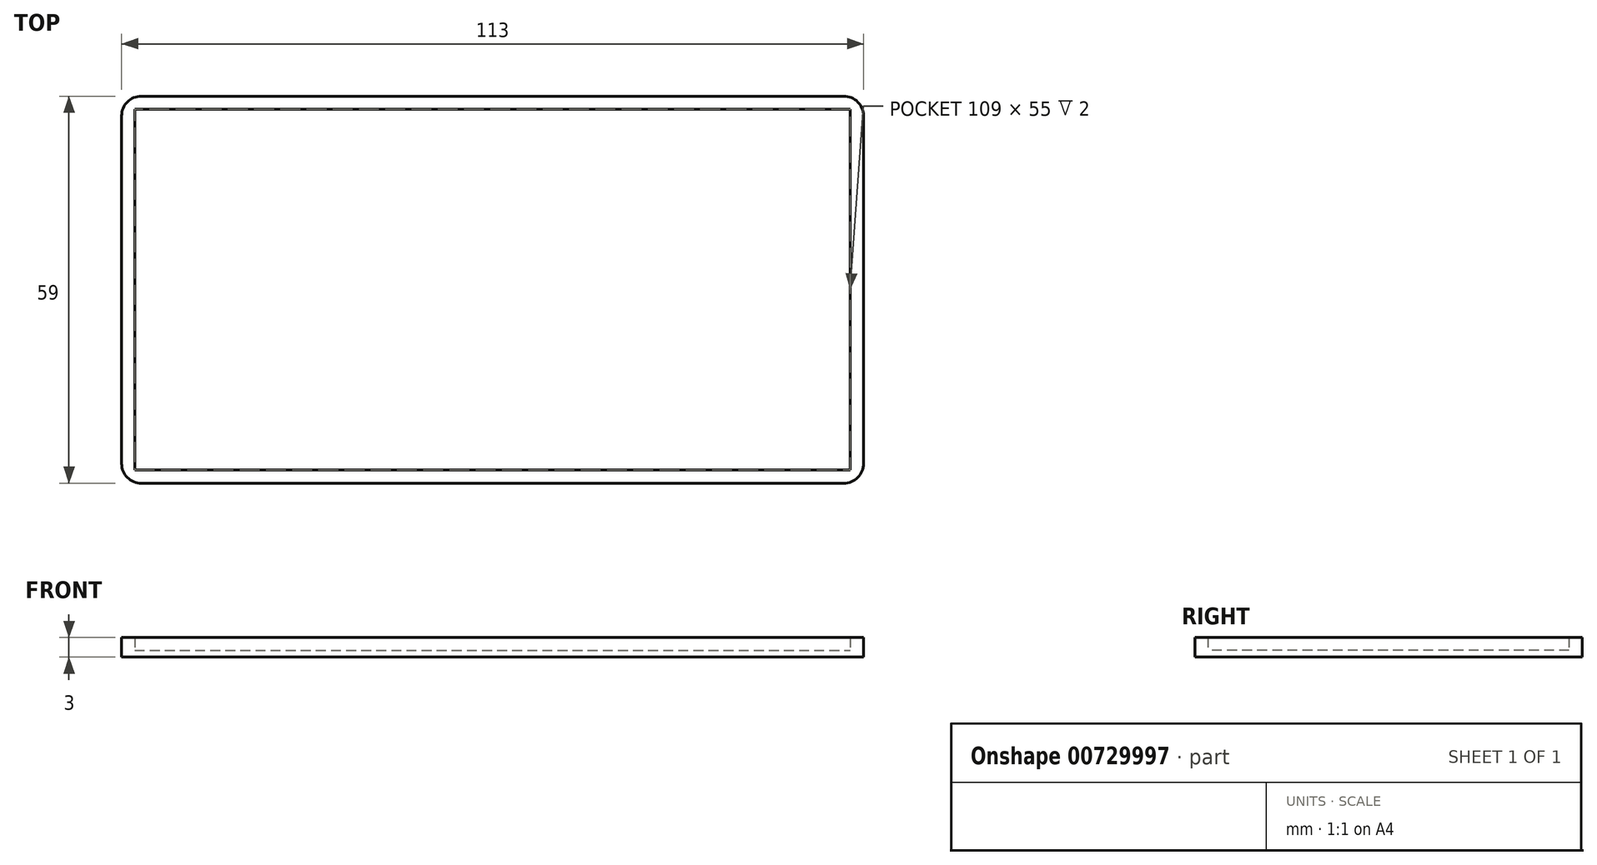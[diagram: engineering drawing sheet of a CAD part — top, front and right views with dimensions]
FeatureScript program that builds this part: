
annotation { "Feature Type Name" : "Feature", "Feature Type Description" : "" }
export const myFeature = defineFeature(function(context is Context, id is Id, definition is map)
    precondition{}
    {
        {
            var Q0;
            Q0=qCreatedBy(makeId("Top.planeOp"),FACE);
            var sketch = newSketch(context, id + "F0", { "sketchPlane" : qUnion([Q0])});
            skLineSegment(sketch, "E0.bottom", {"start": v(-54.5, 23.85) * mm, "end": v(54.5, 23.85) * mm});
            skLineSegment(sketch, "E0.top", {"start": v(-54.5, -31.15) * mm, "end": v(54.5, -31.15) * mm});
            skLineSegment(sketch, "E0.left", {"start": v(-54.5, 23.85) * mm, "end": v(-54.5, -31.15) * mm});
            skLineSegment(sketch, "E0.right", {"start": v(54.5, 23.85) * mm, "end": v(54.5, -31.15) * mm});
            skLineSegment(sketch, "E1.bottom", {"start": v(-56.5, 25.85) * mm, "end": v(56.5, 25.85) * mm});
            skLineSegment(sketch, "E1.top", {"start": v(-56.5, -33.15) * mm, "end": v(56.5, -33.15) * mm});
            skLineSegment(sketch, "E1.left", {"start": v(-56.5, 25.85) * mm, "end": v(-56.5, -33.15) * mm});
            skLineSegment(sketch, "E1.right", {"start": v(56.5, 25.85) * mm, "end": v(56.5, -33.15) * mm});
            skArc(sketch, "E2", {"start": v(-10, -33.15) * mm, "mid": v(0, -43.15) * mm, "end": v(10, -33.15) * mm});
            skArc(sketch, "E3", {"start": v(-11, -33.15) * mm, "mid": v(0, -44.15) * mm, "end": v(11, -33.15) * mm});
            skSolve(sketch);
        }
        {
            var Q0;
            Q0=makeQuery(id+"F0.imprint","IMPRINT",FACE,{"disambiguationData":[TD([[makeQuery(id+"F0.imprint","IMPRINT",EDGE,{"derivedFrom":sQuery(id+"F0.wireOp",EDGE,"E0.bottom")}),-1.0]])]});
            extrude(context, id + "F1", {"entities" : qUnion([Q0]), "depth" : 1 * mm, "offsetDistance" : 25 * mm});
        }
        {
            var Q0;
            Q0=makeQuery(id+"F0.imprint","IMPRINT",FACE,{"disambiguationData":[TD([[makeQuery(id+"F0.imprint","IMPRINT",EDGE,{"derivedFrom":sQuery(id+"F0.wireOp",EDGE,"E0.bottom")}),1.0]])]});
            extrude(context, id + "F2", {"entities" : qUnion([Q0]), "operationType" : NewBodyOperationType.ADD, "depth" : 3 * mm, "offsetDistance" : 25 * mm});
        }
        {
            var Q0;
            Q0=makeQuery(id+"F2.opExtrude","SWEPT_EDGE",EDGE,{"disambiguationData":[OSD([sQuery(id+"F0.wireOp",EDGE,"E1.bottom"),sQuery(id+"F0.wireOp",EDGE,"E1.left")])]});
            var Q1;
            Q1=makeQuery(id+"F2.opExtrude","SWEPT_EDGE",EDGE,{"disambiguationData":[OSD([sQuery(id+"F0.wireOp",EDGE,"E1.top"),sQuery(id+"F0.wireOp",EDGE,"E1.left")])]});
            var Q2;
            Q2=makeQuery(id+"F2.opExtrude","SWEPT_EDGE",EDGE,{"disambiguationData":[OSD([sQuery(id+"F0.wireOp",EDGE,"E1.top"),sQuery(id+"F0.wireOp",EDGE,"E1.right")])]});
            var Q3;
            Q3=makeQuery(id+"F2.opExtrude","SWEPT_EDGE",EDGE,{"disambiguationData":[OSD([sQuery(id+"F0.wireOp",EDGE,"E1.bottom"),sQuery(id+"F0.wireOp",EDGE,"E1.right")])]});
            fillet(context, id + "F3", {"entities" : qUnion([Q0, Q1, Q2, Q3]), "radius" : 3 * mm, "tangentPropagation" : true, "allowEdgeOverflow" : false});
        }
    });
